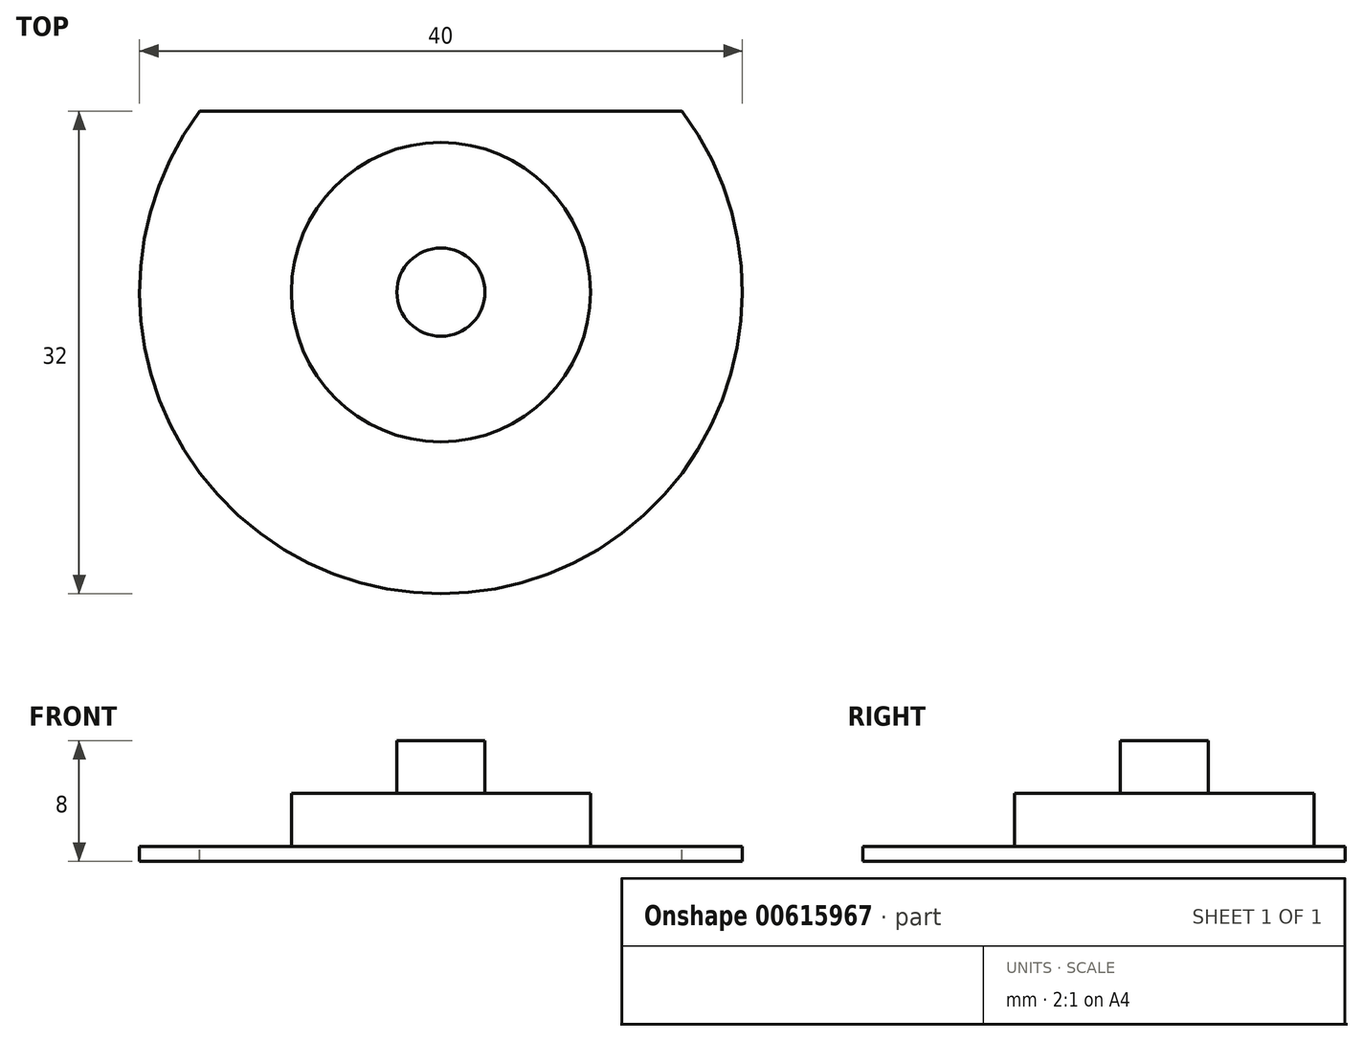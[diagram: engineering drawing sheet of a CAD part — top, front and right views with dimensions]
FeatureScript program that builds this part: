
annotation { "Feature Type Name" : "Feature", "Feature Type Description" : "" }
export const myFeature = defineFeature(function(context is Context, id is Id, definition is map)
    precondition{}
    {
        {
            var Q0;
            Q0=qCreatedBy(makeId("Top.planeOp"),FACE);
            var sketch = newSketch(context, id + "F0", { "sketchPlane" : qUnion([Q0])});
            skCircle(sketch, "E0", {"center": v(0, 0) * mm, "radius": 20 * mm});
            skSolve(sketch);
        }
        {
            var Q0;
            Q0=qSketchRegion(id+"F0",true);
            extrude(context, id + "F1", {"entities" : qUnion([Q0]), "depth" : 1 * mm, "offsetDistance" : 25 * mm});
        }
        {
            var Q0;
            Q0=makeQuery(id+"F1.opExtrude","CAP_FACE",FACE,{"disambiguationData":[OSD([sQuery(id+"F0.wireOp",EDGE,"E0")])],"isStart":false});
            var sketch = newSketch(context, id + "F2", { "sketchPlane" : qUnion([Q0])});
            skCircle(sketch, "E1", {"center": v(0, 0) * mm, "radius": 9.93 * mm});
            skSolve(sketch);
        }
        {
            var Q0;
            Q0=qSketchRegion(id+"F2",true);
            extrude(context, id + "F3", {"entities" : qUnion([Q0]), "operationType" : NewBodyOperationType.ADD, "depth" : 3.5 * mm, "offsetDistance" : 25 * mm});
        }
        {
            var Q0;
            Q0=makeQuery(id+"F3.opExtrude","CAP_FACE",FACE,{"disambiguationData":[OSD([sQuery(id+"F2.wireOp",EDGE,"E1")])],"isStart":false});
            var sketch = newSketch(context, id + "F4", { "sketchPlane" : qUnion([Q0])});
            skCircle(sketch, "E2", {"center": v(0, 0) * mm, "radius": 2.93 * mm});
            skSolve(sketch);
        }
        {
            var Q0;
            Q0=makeQuery(id+"F4.imprint","IMPRINT",FACE,{"disambiguationData":[TD([[makeQuery(id+"F4.imprint","IMPRINT",EDGE,{"derivedFrom":sQuery(id+"F4.wireOp",EDGE,"E2")}),1.0]])]});
            extrude(context, id + "F5", {"entities" : qUnion([Q0]), "operationType" : NewBodyOperationType.ADD, "depth" : 3.5 * mm, "offsetDistance" : 25 * mm});
        }
        {
            var Q0;
            Q0=makeQuery(id+"F1.opExtrude","CAP_FACE",FACE,{"disambiguationData":[OSD([sQuery(id+"F0.wireOp",EDGE,"E0")])],"isStart":false});
            var sketch = newSketch(context, id + "F6", { "sketchPlane" : qUnion([Q0])});
            skLineSegment(sketch, "E3", {"start": v(0, 0) * mm, "end": v(0, 12) * mm, "construction": true});
            skLineSegment(sketch, "E4.bottom", {"start": v(0, 12) * mm, "end": v(16, 12) * mm});
            skLineSegment(sketch, "E4.top", {"start": v(0, 21) * mm, "end": v(16, 21) * mm});
            skLineSegment(sketch, "E4.left", {"start": v(0, 12) * mm, "end": v(0, 21) * mm});
            skLineSegment(sketch, "E4.right", {"start": v(16, 12) * mm, "end": v(16, 21) * mm});
            skLineSegment(sketch, "E5.bottom", {"start": v(0, 12) * mm, "end": v(-16, 12) * mm});
            skLineSegment(sketch, "E5.top", {"start": v(0, 21) * mm, "end": v(-16, 21) * mm});
            skLineSegment(sketch, "E5.right", {"start": v(-16, 12) * mm, "end": v(-16, 21) * mm});
            skSolve(sketch);
        }
        {
            var Q0;
            Q0 = qSketchRegion(id + "F6", true);
            extrude(context, id + "F7", {"entities" : qUnion([Q0]), "operationType" : NewBodyOperationType.REMOVE, "oppositeDirection" : true, "depth" : 25 * mm, "offsetDistance" : 25 * mm});
        }
    });
